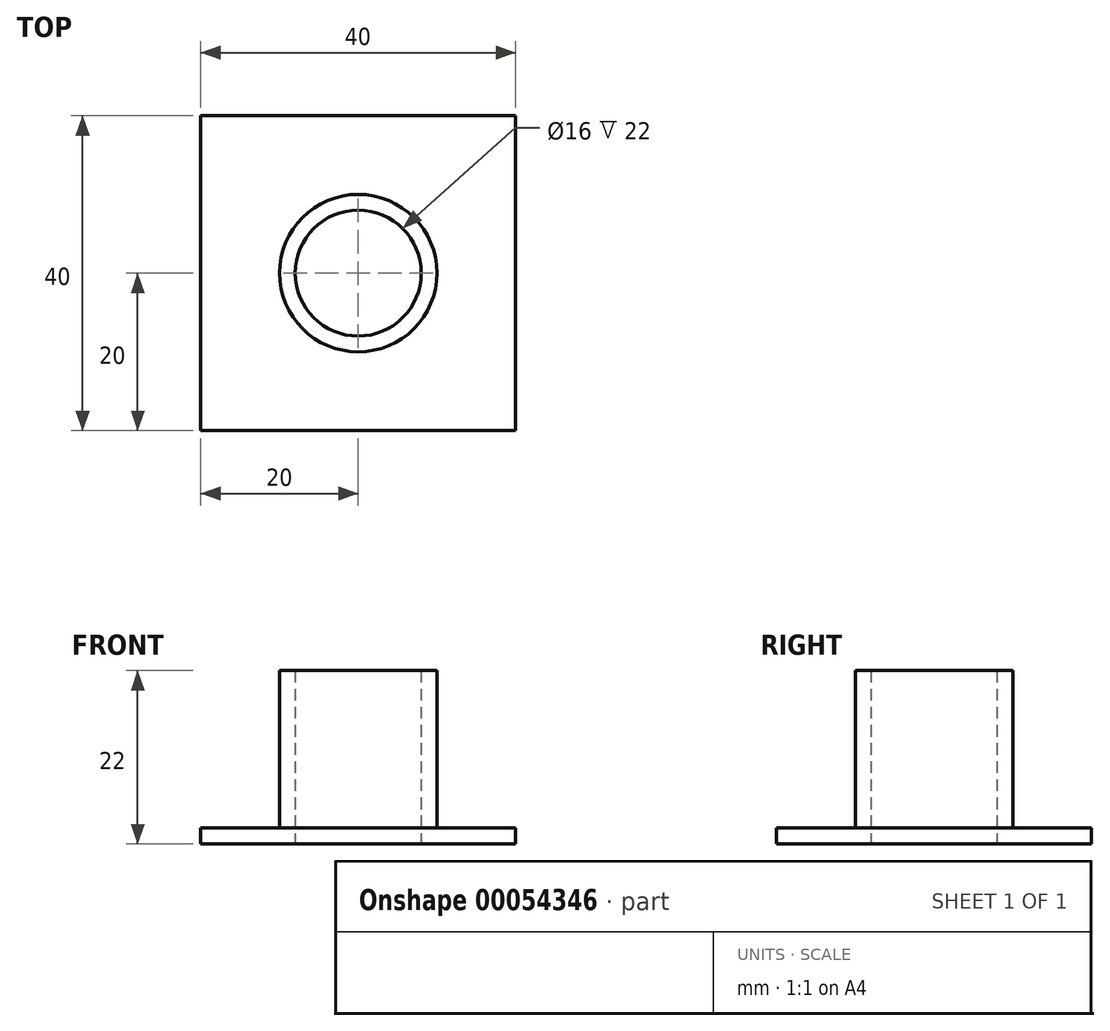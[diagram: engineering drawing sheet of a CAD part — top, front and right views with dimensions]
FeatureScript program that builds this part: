
annotation { "Feature Type Name" : "Feature", "Feature Type Description" : "" }
export const myFeature = defineFeature(function(context is Context, id is Id, definition is map)
    precondition{}
    {
        {
            var Q0;
            Q0=qCreatedBy(makeId("Top.planeOp"),FACE);
            var sketch = newSketch(context, id + "F0", { "sketchPlane" : qUnion([Q0])});
            skLineSegment(sketch, "E0.rect.bottom", {"start": v(-20, 20) * mm, "end": v(20, 20) * mm});
            skLineSegment(sketch, "E0.rect.top", {"start": v(-20, -20) * mm, "end": v(20, -20) * mm});
            skLineSegment(sketch, "E0.rect.left", {"start": v(-20, 20) * mm, "end": v(-20, -20) * mm});
            skLineSegment(sketch, "E0.rect.right", {"start": v(20, 20) * mm, "end": v(20, -20) * mm});
            skPoint(sketch, "E0.rect.middle", {"position": v(0, 0) * mm});
            skCircle(sketch, "E1", {"center": v(0, 0) * mm, "radius": 10 * mm});
            skCircle(sketch, "E2", {"center": v(0, 0) * mm, "radius": 8 * mm});
            skSolve(sketch);
        }
        {
            var Q0;
            Q0=makeQuery(id+"F0.imprint","IMPRINT",FACE,{"disambiguationData":[TD([[makeQuery(id+"F0.imprint","IMPRINT",EDGE,{"derivedFrom":sQuery(id+"F0.wireOp",EDGE,"E0.rect.bottom")}),-1.0]])]});
            extrude(context, id + "F1", {"entities" : qUnion([Q0]), "depth" : 2 * mm});
        }
        {
            var Q0;
            Q0=makeQuery(id+"F0.imprint","IMPRINT",FACE,{"disambiguationData":[TD([[makeQuery(id+"F0.imprint","IMPRINT",EDGE,{"derivedFrom":sQuery(id+"F0.wireOp",EDGE,"E1")}),1.0]])]});
            extrude(context, id + "F2", {"entities" : qUnion([Q0]), "operationType" : NewBodyOperationType.ADD, "depth" : 22 * mm});
        }
    });
